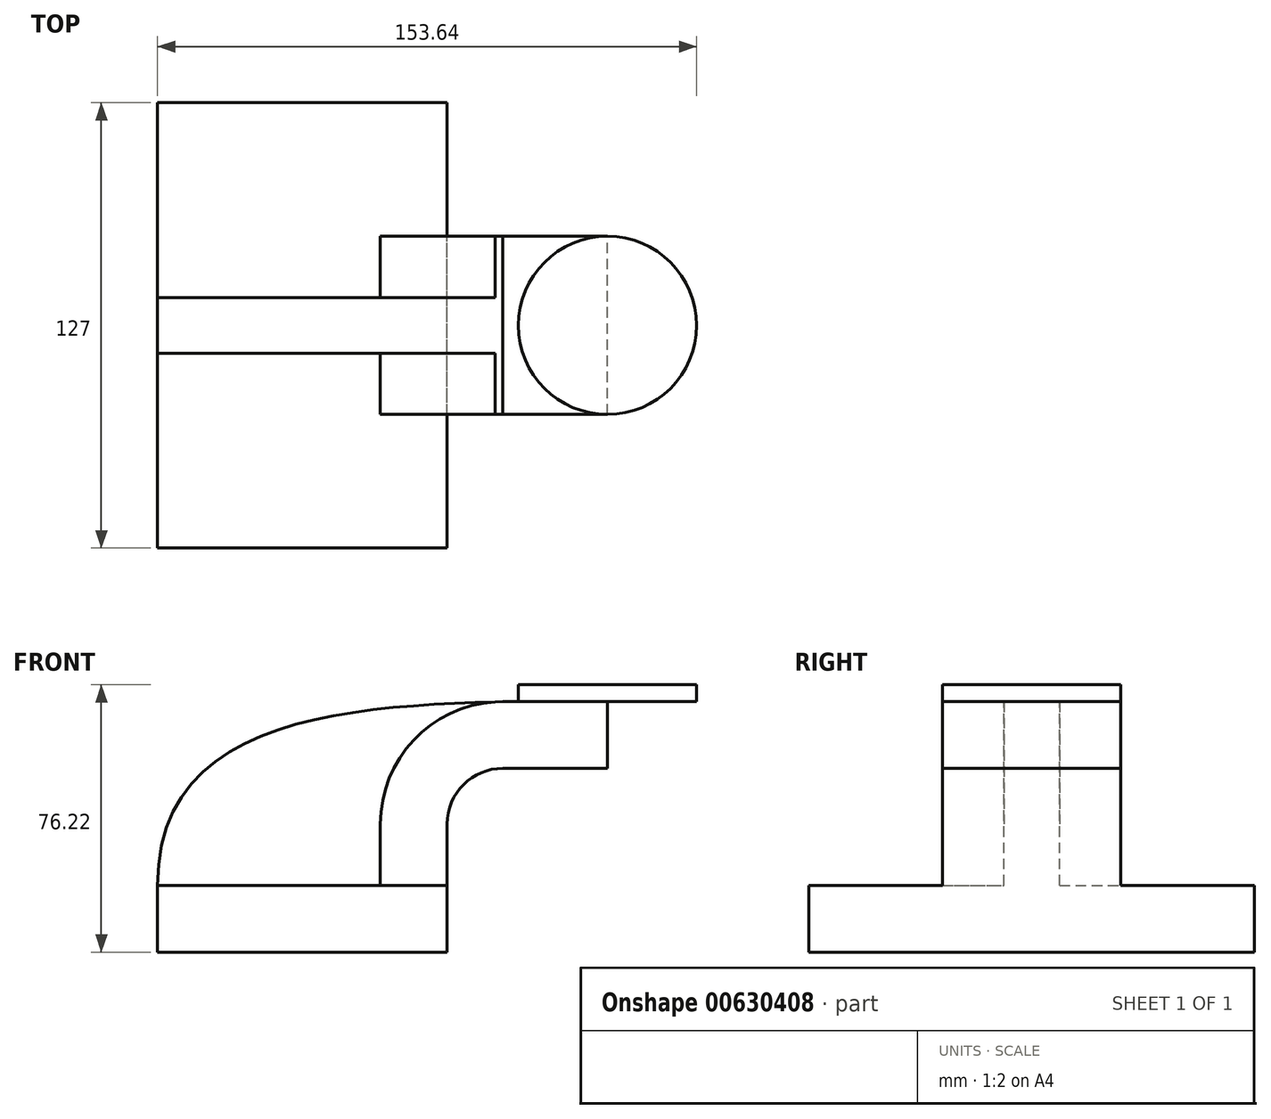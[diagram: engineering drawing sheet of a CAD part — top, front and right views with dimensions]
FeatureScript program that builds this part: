
annotation { "Feature Type Name" : "Feature", "Feature Type Description" : "" }
export const myFeature = defineFeature(function(context is Context, id is Id, definition is map)
    precondition{}
    {
        {
            var Q0;
            Q0=qCreatedBy(makeId("Front.planeOp"),FACE);
            var sketch = newSketch(context, id + "F0", { "sketchPlane" : qUnion([Q0])});
            skLineSegment(sketch, "E0.bottom", {"start": v(-41.28, -9.53) * mm, "end": v(41.28, -9.53) * mm});
            skLineSegment(sketch, "E0.top", {"start": v(-41.28, 9.53) * mm, "end": v(41.28, 9.53) * mm});
            skLineSegment(sketch, "E0.left", {"start": v(-41.28, -9.53) * mm, "end": v(-41.28, 9.53) * mm});
            skLineSegment(sketch, "E0.right", {"start": v(41.28, -9.53) * mm, "end": v(41.28, 9.53) * mm});
            skPoint(sketch, "E0.middle", {"position": v(0, 0) * mm});
            skLineSegment(sketch, "E1.bottom", {"start": v(60.32, 38.1) * mm, "end": v(111.12, 38.1) * mm});
            skLineSegment(sketch, "E1.top", {"start": v(60.32, 66.67) * mm, "end": v(111.12, 66.67) * mm});
            skLineSegment(sketch, "E1.left", {"start": v(60.32, 38.1) * mm, "end": v(60.32, 66.67) * mm});
            skLineSegment(sketch, "E1.right", {"start": v(111.12, 38.1) * mm, "end": v(111.12, 66.67) * mm});
            skPoint(sketch, "E1.middle", {"position": v(85.72, 52.39) * mm});
            skLineSegment(sketch, "E2", {"start": v(41.28, 9.53) * mm, "end": v(41.28, 27) * mm});
            skArc(sketch, "E3", {"start": v(41.27, 27) * mm, "mid": v(45.92, 38.23) * mm, "end": v(57.15, 42.88) * mm});
            skLineSegment(sketch, "E4", {"start": v(57.15, 42.88) * mm, "end": v(86.96, 42.88) * mm});
            skLineSegment(sketch, "E5.0", {"start": v(57.15, 61.93) * mm, "end": v(86.96, 61.93) * mm});
            skArc(sketch, "E5.1", {"start": v(22.22, 27) * mm, "mid": v(32.45, 51.7) * mm, "end": v(57.15, 61.93) * mm});
            skLineSegment(sketch, "E5.2", {"start": v(22.23, 9.53) * mm, "end": v(22.23, 27) * mm});
            skLineSegment(sketch, "E6", {"start": v(86.96, 42.88) * mm, "end": v(86.96, 61.93) * mm});
            skFitSpline(sketch, "E7", {"points": [v(-41.28, 9.53) * mm, v(57.15, 61.93) * mm], "startDerivative": vector(-0.5, 144.76) * mm, "endDerivative": vector(131.33, 4.13) * mm});
            skSolve(sketch);
        }
        {
            var Q0;
            Q0=makeQuery(id+"F0.imprint","IMPRINT",FACE,{"disambiguationData":[TD([[makeQuery(id+"F0.imprint","IMPRINT",EDGE,{"derivedFrom":sQuery(id+"F0.wireOp",EDGE,"E0.bottom")}),1.0]])]});
            extrude(context, id + "F1", {"entities" : qUnion([Q0]), "endBound" : BoundingType.SYMMETRIC, "depth" : 127 * mm, "offsetDistance" : 25.4 * mm});
        }
        {
            var Q0;
            {var subQ0=sQuery(id+"F0.wireOp",EDGE,"E2");Q0=makeQuery(id+"F0.imprint","IMPRINT",FACE,{"disambiguationData":[TD([[makeQuery(id+"F0.imprint","IMPRINT",EDGE,{"derivedFrom":subQ0}),1.0]])]});}
            var Q1;
            {var subQ5=sQuery(id+"F0.wireOp",EDGE,"E6");Q1=makeQuery(id+"F0.imprint","IMPRINT",FACE,{"disambiguationData":[TD([[makeQuery(id+"F0.imprint","IMPRINT",EDGE,{"derivedFrom":subQ5}),1.0]])]});}
            extrude(context, id + "F2", {"entities" : qUnion([Q0, Q1]), "operationType" : NewBodyOperationType.ADD, "endBound" : BoundingType.SYMMETRIC, "depth" : 50.8 * mm, "offsetDistance" : 25.4 * mm});
        }
        {
            var Q0;
            {var subQ3=sQuery(id+"F0.wireOp",EDGE,"E5.2");Q0=makeQuery(id+"F0.imprint","IMPRINT",FACE,{"disambiguationData":[TD([[makeQuery(id+"F0.imprint","IMPRINT",EDGE,{"derivedFrom":subQ3}),1.0]])]});}
            extrude(context, id + "F3", {"entities" : qUnion([Q0]), "operationType" : NewBodyOperationType.ADD, "endBound" : BoundingType.SYMMETRIC, "depth" : 15.88 * mm, "offsetDistance" : 25.4 * mm});
        }
        {
            var Q0;
            Q0=makeQuery(id+"F2.opExtrude","SWEPT_FACE",FACE,{"disambiguationData":[OSD([sQuery(id+"F0.wireOp",EDGE,"E5.0")])]});
            var sketch = newSketch(context, id + "F4", { "sketchPlane" : qUnion([Q0])});
            skCircle(sketch, "E8", {"center": v(86.96, 0) * mm, "radius": 25.4 * mm});
            skSolve(sketch);
        }
        {
            var Q0;
            {var subQ1=sQuery(id+"F0.wireOp",EDGE,"E5.0");var subQ2=makeQuery(id+"F2.opExtrude","SWEPT_EDGE",EDGE,{"disambiguationData":[OSD([subQ1,sQuery(id+"F0.wireOp",EDGE,"E6")])]});Q0=makeQuery(id+"F4.imprint","IMPRINT",FACE,{"disambiguationData":[TD([[makeQuery(id+"F4.imprint","IMPRINT",EDGE,{"derivedFrom":subQ2}),1.0]])]});}
            var Q1;
            {var subQ1=sQuery(id+"F0.wireOp",EDGE,"E5.0");var subQ2=makeQuery(id+"F2.opExtrude","SWEPT_EDGE",EDGE,{"disambiguationData":[OSD([subQ1,sQuery(id+"F0.wireOp",EDGE,"E6")])]});Q1=makeQuery(id+"F4.imprint","IMPRINT",FACE,{"disambiguationData":[TD([[makeQuery(id+"F4.imprint","IMPRINT",EDGE,{"derivedFrom":subQ2}),-1.0]])]});}
            extrude(context, id + "F5", {"entities" : qUnion([Q0, Q1]), "operationType" : NewBodyOperationType.ADD, "depth" : 4.76 * mm, "offsetDistance" : 25.4 * mm});
        }
    });
